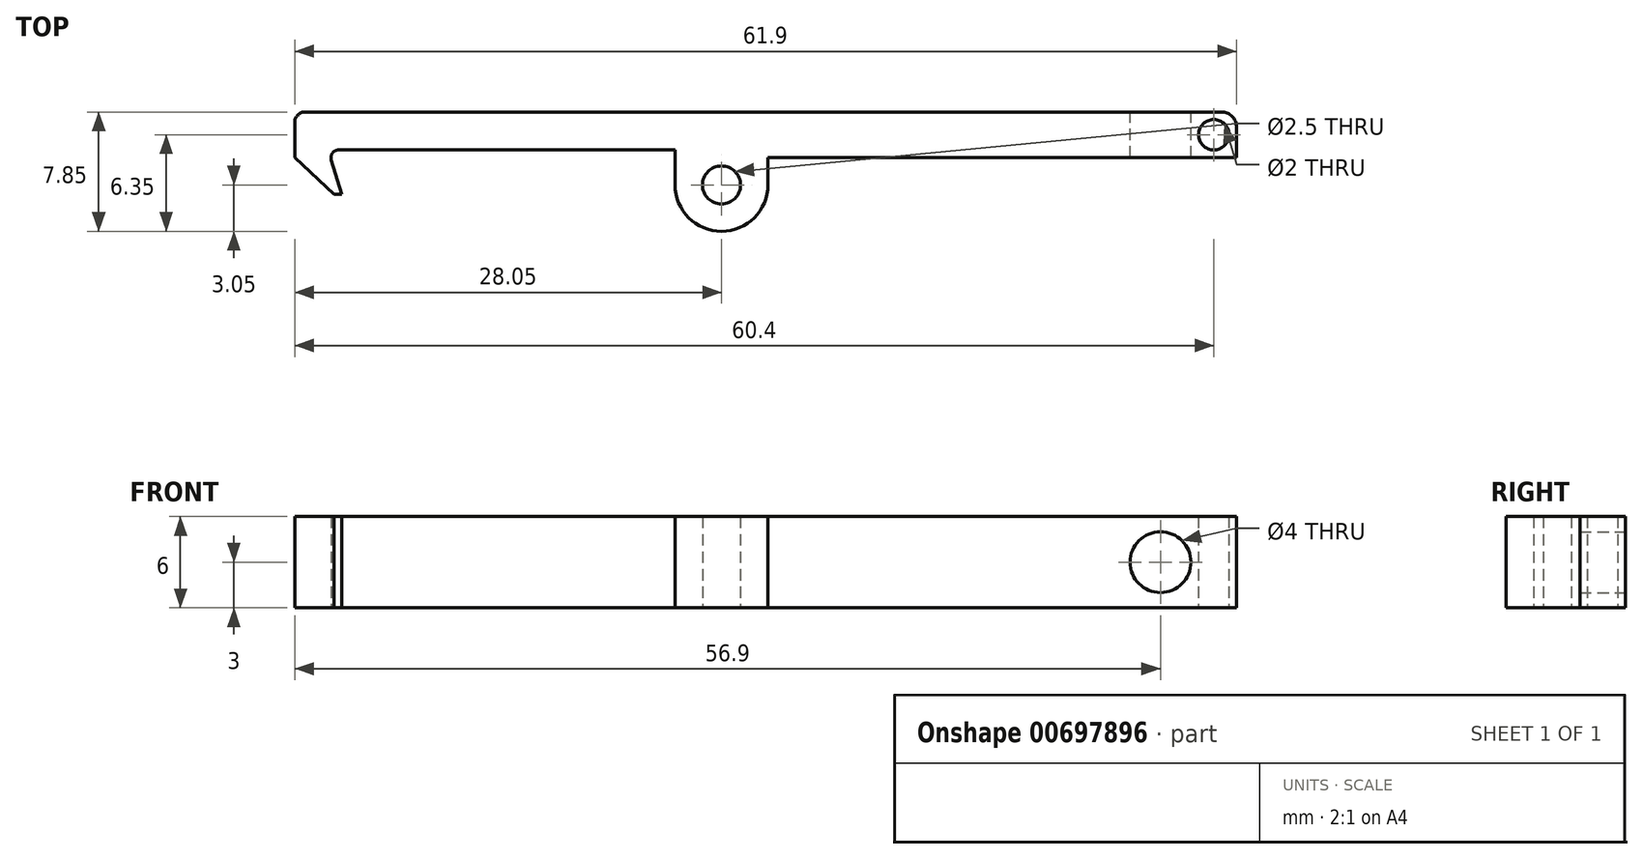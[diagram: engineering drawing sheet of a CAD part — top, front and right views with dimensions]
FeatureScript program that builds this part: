
annotation { "Feature Type Name" : "Feature", "Feature Type Description" : "" }
export const myFeature = defineFeature(function(context is Context, id is Id, definition is map)
    precondition{}
    {
        {
            var Q0;
            Q0=qCreatedBy(makeId("Top.planeOp"),FACE);
            var sketch = newSketch(context, id + "F0", { "sketchPlane" : qUnion([Q0])});
            skLineSegment(sketch, "E0.bottom", {"start": v(-30.4, 3) * mm, "end": v(29.8, 3) * mm});
            skLineSegment(sketch, "E0.left", {"start": v(-31.1, 2.3) * mm, "end": v(-31.1, 0) * mm});
            skLineSegment(sketch, "E0.right", {"start": v(30.8, 2) * mm, "end": v(30.8, 0) * mm});
            skLineSegment(sketch, "E1", {"start": v(-31.1, 0) * mm, "end": v(-31.1, 0) * mm});
            skLineSegment(sketch, "E2.trimOffspring", {"start": v(0, 0) * mm, "end": v(30.8, 0) * mm});
            skPoint(sketch, "E3.visualSharp", {"position": v(-31.1, 3) * mm});
            skArc(sketch, "E3.filletArc", {"start": v(-30.4, 3) * mm, "mid": v(-30.9, 2.8) * mm, "end": v(-31.1, 2.3) * mm});
            skLineSegment(sketch, "E4.left", {"start": v(-6.1, 0.5) * mm, "end": v(-6.1, -1.8) * mm});
            skLineSegment(sketch, "E4.right", {"start": v(0, 0) * mm, "end": v(0, -1.8) * mm});
            skCircle(sketch, "E5", {"center": v(-3.05, -1.8) * mm, "radius": 1.25 * mm});
            skArc(sketch, "E6", {"start": v(0, -1.8) * mm, "mid": v(-3.05, -4.85) * mm, "end": v(-6.1, -1.8) * mm});
            skLineSegment(sketch, "E7", {"start": v(-31.1, 0) * mm, "end": v(-28.5, -2.4) * mm});
            skLineSegment(sketch, "E8", {"start": v(-28.5, -2.4) * mm, "end": v(-28, -2.4) * mm});
            skLineSegment(sketch, "E9", {"start": v(-28.21, 0.5) * mm, "end": v(-6.1, 0.5) * mm});
            skLineSegment(sketch, "E10", {"start": v(-28.7, -0.15) * mm, "end": v(-28, -2.4) * mm});
            skCircle(sketch, "E11", {"center": v(29.3, 1.5) * mm, "radius": 1 * mm});
            skPoint(sketch, "E11.centerSnap0", {"position": v(30.8, 1.5) * mm});
            skPoint(sketch, "E12.visualSharp", {"position": v(30.8, 3) * mm});
            skArc(sketch, "E12.filletArc", {"start": v(30.8, 2) * mm, "mid": v(30.5, 2.7) * mm, "end": v(29.8, 3) * mm});
            skPoint(sketch, "E13.visualSharp", {"position": v(-28.89, 0.5) * mm});
            skArc(sketch, "E13.filletArc", {"start": v(-28.21, 0.5) * mm, "mid": v(-28.62, 0.3) * mm, "end": v(-28.7, -0.15) * mm});
            skSolve(sketch);
        }
        {
            var Q0;
            Q0=makeQuery(id+"F0.imprint","IMPRINT",FACE,{"disambiguationData":[TD([[makeQuery(id+"F0.imprint","IMPRINT",EDGE,{"derivedFrom":sQuery(id+"F0.wireOp",EDGE,"E0.bottom")}),-1.0]])]});
            extrude(context, id + "F1", {"entities" : qUnion([Q0]), "depth" : 6 * mm, "offsetDistance" : 25 * mm});
        }
        {
            var Q0;
            Q0=makeQuery(id+"F1.opExtrude","SWEPT_FACE",FACE,{"disambiguationData":[OSD([sQuery(id+"F0.wireOp",EDGE,"E0.bottom")])]});
            var sketch = newSketch(context, id + "F2", { "sketchPlane" : qUnion([Q0])});
            skPoint(sketch, "E14", {"position": v(-25.8, 3) * mm});
            skPoint(sketch, "E14.positionSnap0", {"position": v(-29.8, 3) * mm});
            skSolve(sketch);
        }
        {
            var Q0;
            Q0=sQuery(id+"F2.wireOp",VERTEX,"E14");
            var Q1;
            Q1=makeQuery(id+"F1.opExtrude","SWEPT_BODY",BODY,{"disambiguationData":[OSD([sQuery(id+"F0.wireOp",EDGE,"E0.bottom"),sQuery(id+"F0.wireOp",EDGE,"E0.left"),sQuery(id+"F0.wireOp",EDGE,"E0.right"),sQuery(id+"F0.wireOp",EDGE,"E2.trimOffspring"),sQuery(id+"F0.wireOp",EDGE,"E3.filletArc"),sQuery(id+"F0.wireOp",EDGE,"E4.left"),sQuery(id+"F0.wireOp",EDGE,"E4.right"),sQuery(id+"F0.wireOp",EDGE,"E5"),sQuery(id+"F0.wireOp",EDGE,"E6"),sQuery(id+"F0.wireOp",EDGE,"E7"),sQuery(id+"F0.wireOp",EDGE,"E8"),sQuery(id+"F0.wireOp",EDGE,"E9"),sQuery(id+"F0.wireOp",EDGE,"E10"),sQuery(id+"F0.wireOp",EDGE,"E11"),sQuery(id+"F0.wireOp",EDGE,"E12.filletArc")])]});
            hole(context, id + "F3", {"style" : HoleStyle.SIMPLE, "endStyle" : HoleEndStyle.THROUGH, "holeDiameter" : 4 * mm, "majorDiameter" : 5 * mm, "isTappedThrough" : true, "tappedDepth" : 12 * mm, "tapClearance" : 3, "locations" : qUnion([Q0]), "scope" : qUnion([Q1])});
        }
    });
